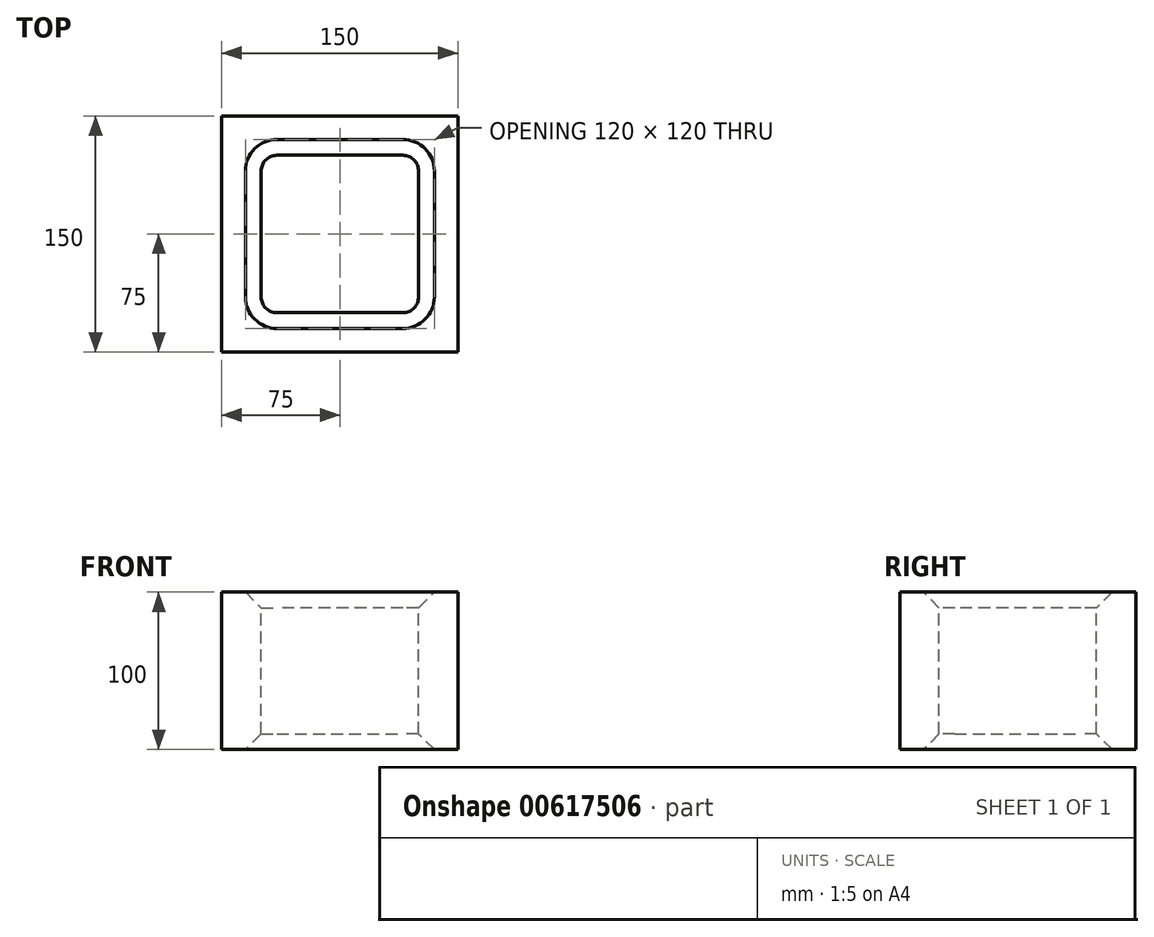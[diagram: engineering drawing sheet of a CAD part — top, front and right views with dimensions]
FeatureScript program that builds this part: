
annotation { "Feature Type Name" : "Feature", "Feature Type Description" : "" }
export const myFeature = defineFeature(function(context is Context, id is Id, definition is map)
    precondition{}
    {
        {
            var Q0;
            Q0=qCreatedBy(makeId("Top.planeOp"),FACE);
            var sketch = newSketch(context, id + "F0", { "sketchPlane" : qUnion([Q0])});
            skLineSegment(sketch, "E0.bottom", {"start": v(40, -50) * mm, "end": v(-40, -50) * mm});
            skLineSegment(sketch, "E0.top", {"start": v(40, 50) * mm, "end": v(-40, 50) * mm});
            skLineSegment(sketch, "E0.left", {"start": v(50, -40) * mm, "end": v(50, 40) * mm});
            skLineSegment(sketch, "E0.right", {"start": v(-50, -40) * mm, "end": v(-50, 40) * mm});
            skPoint(sketch, "E0.middle", {"position": v(0, 0) * mm});
            skPoint(sketch, "E1.visualSharp", {"position": v(-50, 50) * mm});
            skArc(sketch, "E1.filletArc", {"start": v(-40, 50) * mm, "mid": v(-47.07, 47.07) * mm, "end": v(-50, 40) * mm});
            skPoint(sketch, "E2.visualSharp", {"position": v(-50, -50) * mm});
            skArc(sketch, "E2.filletArc", {"start": v(-50, -40) * mm, "mid": v(-47.07, -47.07) * mm, "end": v(-40, -50) * mm});
            skPoint(sketch, "E3.visualSharp", {"position": v(50, -50) * mm});
            skArc(sketch, "E3.filletArc", {"start": v(40, -50) * mm, "mid": v(47.07, -47.07) * mm, "end": v(50, -40) * mm});
            skPoint(sketch, "E4.visualSharp", {"position": v(50, 50) * mm});
            skArc(sketch, "E4.filletArc", {"start": v(50, 40) * mm, "mid": v(47.07, 47.07) * mm, "end": v(40, 50) * mm});
            skLineSegment(sketch, "E5.bottom", {"start": v(75, -75) * mm, "end": v(-75, -75) * mm});
            skLineSegment(sketch, "E5.top", {"start": v(75, 75) * mm, "end": v(-75, 75) * mm});
            skLineSegment(sketch, "E5.left", {"start": v(75, -75) * mm, "end": v(75, 75) * mm});
            skLineSegment(sketch, "E5.right", {"start": v(-75, -75) * mm, "end": v(-75, 75) * mm});
            skSolve(sketch);
        }
        {
            var Q0;
            Q0=makeQuery(id+"F0.imprint","IMPRINT",FACE,{"disambiguationData":[TD([[makeQuery(id+"F0.imprint","IMPRINT",EDGE,{"derivedFrom":sQuery(id+"F0.wireOp",EDGE,"E0.bottom")}),1.0]])]});
            extrude(context, id + "F1", {"entities" : qUnion([Q0]), "oppositeDirection" : true, "depth" : 100 * mm, "offsetDistance" : 25 * mm});
        }
        {
            var Q0;
            Q0=makeQuery(id+"F1.opExtrude","CAP_EDGE",EDGE,{"disambiguationData":[OSD([sQuery(id+"F0.wireOp",EDGE,"E0.right")])],"isStart":true});
            chamfer(context, id + "F2", {"entities" : qUnion([Q0]), "width" : 10 * mm, "tangentPropagation" : true});
        }
        {
            var Q0;
            Q0=makeQuery(id+"F1.opExtrude","CAP_EDGE",EDGE,{"disambiguationData":[OSD([sQuery(id+"F0.wireOp",EDGE,"E0.left")])],"isStart":false});
            chamfer(context, id + "F3", {"entities" : qUnion([Q0]), "width" : 10 * mm, "tangentPropagation" : true});
        }
    });
